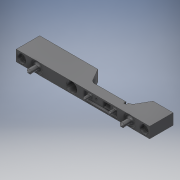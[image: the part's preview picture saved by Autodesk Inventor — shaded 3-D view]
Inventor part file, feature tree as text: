
AUTODESK INVENTOR PART (.ipt)
format: ipt  version: 2018 (Build 220112000, 112)  size: 404,480 bytes
history: native  units: mm
features: sketch x19, extrude x14, projected_geometry x14, hole x5, chamfer x3, fillet x3, draft x2, plane x1
ambient origin geometry x8: Origin, YZ Plane, XZ Plane, XY Plane, X Axis, Y Axis, Z Axis, Center Point
bodies: Solid1 (feature_tree)
feature tree (61):
  extrude  "Extrusion1"  Depth=7.0mm
  extrude  "Extrusion2"  Depth=4.2mm
  extrude  "Extrusion3"  Depth=6.4mm
  extrude  "Extrusion4"  Depth=0.7mm
  extrude  "Extrusion5"  Depth=5.2mm
  hole  "Hole1"  [1 undecoded]
  hole  "Hole2"  [1 undecoded]
  extrude  "Extrusion8"  Depth=2.4mm
  chamfer  "Chamfer1"  Distance=2.4mm
  plane  "Work Plane2"
  fillet  "Fillet1"  Radius=3.5mm
  extrude  "Extrusion10"  Depth=3.5mm
  hole  "Hole3"  [1 undecoded]
  extrude  "Extrusion11"  Depth=1.0mm TaperAngle=0.0deg
  chamfer  "Chamfer3"  Distance=1.0mm Angle=45.0deg
  chamfer  "Chamfer4"  Distance=0.8mm
  extrude  "Extrusion12"  Depth=71.4mm
  extrude  "Extrusion14"  Depth=28.4mm
  hole  "Hole4"  [1 undecoded]
  extrude  "Extrusion15"  Depth=2.8mm
  hole  "Hole5"  [1 undecoded]
  extrude  "Extrusion17"  Depth=1.0mm TaperAngle=0.0deg
  extrude  "Extrusion18"  Depth=7.0mm TaperAngle=0.0deg
  draft  "FaceDraft2"
  draft  "FaceDraft3"
  fillet  "Fillet3"  [1 undecoded]
  extrude  "Extrusion19"  Depth=7.0mm TaperAngle=0.0deg
  fillet  "Fillet4"  [1 undecoded]
  sketch  "Sketch1"  dims[d0=22.8mm d1=7.0mm]
  sketch  "Sketch2"  dims[d2=6.0mm d3=0.0mm d4=4.2mm]
  sketch  "Sketch3"  dims[d5=4.5mm d6=6.4mm]
  projected_geometry  "Projected Loop1"
  sketch  "Sketch4"  dims[d7=6.0mm d8=0.0mm d11=0.7mm]
  projected_geometry  "Projected Loop2"
  sketch  "Sketch5"  dims[d12=0.9mm d13=5.2mm]
  sketch  "Sketch6"  dims[d14=21.2mm d15=1.5mm d16=0.0mm]
  projected_geometry  "Projected Loop3"
  sketch  "Sketch8"  dims[d17=14.0mm d18=2.9mm d19=0.0mm]
  sketch  "Sketch9"  dims[d20=12.9mm d21=5.0mm d22=2.4mm d23=0.0mm]
  sketch  "Sketch13"  dims[d24=0.5mm d25=6.0mm d26=3.023mm d27=2.0mm d28=14.3117mm d29=2.4mm d30=0.0mm d41=3.5mm]
  projected_geometry  "Projected Loop11"
  sketch  "Sketch14"  dims[d42=15.4mm]
  sketch  "Sketch15"  dims[d43=1.181mm d44=3.048mm d45=3.023mm d46=2.0mm d47=14.3117mm d48=4.636mm d49=0.0mm d50=3.5mm]
  projected_geometry  "Projected Loop12"
  sketch  "Sketch16"  dims[d51=16.1mm d52=3.3mm]
  projected_geometry  "Projected Loop13"
  sketch  "Sketch18"  dims[d53=2.0mm d54=4.3mm d55=0.0mm d56=1.0mm d57=2.0mm d58=45.0deg d67=-3.5mm d74=0.8mm]
  projected_geometry  "Projected Loop15"
  sketch  "Sketch19"  dims[d75=38.8mm d76=71.4mm]
  projected_geometry  "Projected Loop16"
  sketch  "Sketch20"  dims[d77=15.0mm d78=0.0mm d79=28.4mm]
  projected_geometry  "Projected Loop17"
  sketch  "Sketch21"  dims[d80=6.5mm d81=6.0mm d82=3.023mm d83=2.0mm d84=14.3117mm d85=12.0mm d86=0.0mm d87=6.0mm]
  projected_geometry  "Projected Loop18"
  sketch  "Sketch23"  dims[d88=65.4mm d89=2.8mm]
  projected_geometry  "Projected Loop20"
  sketch  "Sketch24"  dims[d90=6.0mm d91=0.0mm d92=1.4mm d93=2.0mm d94=45.0deg]
  projected_geometry  "Projected Loop21"
  sketch  "Sketch25"  dims[d95=0.25mm d96=2.0mm d97=45.0deg d98=6.0mm d99=0.0mm d106=7.0mm d107=0.0mm d108=45.0deg d109=2.9mm d110=6.0mm d111=5.5mm d112=2.5mm d113=14.3117mm d114=12.0mm d115=0.0mm d116=7.0mm d117=0.0mm d118=45.0deg d119=2.9mm d120=6.0mm d121=5.5mm d122=2.5mm d123=14.3117mm d124=12.0mm d125=0.0mm d129=1.5mm d130=1.5mm d131=0.0mm d132=18.0mm d133=1.5mm d134=0.0mm d135=30.0deg d136=30.0deg d137=3.0mm d138=6.0mm d139=6.0mm d140=1.0mm d141=0.0mm d142=1.0mm]
  projected_geometry  "Projected Loop22"
  projected_geometry  "Projected Loop23"
note: 7 required parameter values undecoded (feature->parameter linkage not recoverable at this tier; creation-order binding heuristic only, values carry confidence <= 0.55)
